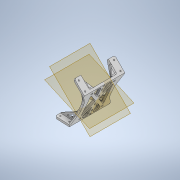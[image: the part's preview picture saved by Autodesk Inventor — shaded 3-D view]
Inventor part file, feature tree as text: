
AUTODESK INVENTOR PART (.ipt)
format: ipt  version: 2023 (Build 270158000, 158)  size: 826,880 bytes
history: native  units: mm
features: projected_geometry x20, sketch x13, extrude x11, fillet x6, reference x6, other x6, mirror x5, plane x4, hole x2, chamfer x1
ambient origin geometry x8: Origin, YZ Plane, XZ Plane, XY Plane, X Axis, Y Axis, Z Axis, Center Point
bodies: Solid1 (feature_tree)
feature tree (74):
  sketch  "Sketch1"  dims[d1=3.0mm d2=22.0mm]
  plane  "Work Plane1"
  extrude  "Extrusion1"  Depth=3.0mm
  hole  "Hole1"  [1 undecoded]
  hole  "Hole2"  [1 undecoded]
  sketch  "Sketch4"  dims[d8=2.0mm d9=6.0mm d10=4.0mm d11=2.0mm d12=90.0deg d13=20.0mm d14=0.0mm]
  plane  "Work Plane2"
  extrude  "Extrusion2"  Depth=10.0mm
  plane  "Work Plane3"
  mirror  "Mirror1"
  extrude  "Extrusion3"  Depth=2.0mm TaperAngle=0.0deg
  mirror  "Mirror2"
  extrude  "Extrusion4"  Depth=10.0mm
  extrude  "Extrusion5"  Depth=10.0mm
  plane  "Work Plane4"
  mirror  "Mirror3"
  chamfer  "Chamfer1"  Distance=2.0mm
  fillet  "Fillet1"  Radius=2.0mm
  extrude  "Extrusion6"  Depth=2.5mm
  fillet  "Fillet2"  Radius=2.5mm
  fillet  "Fillet3"  Radius=2.5mm
  fillet  "Fillet4"  Radius=2.5mm
  fillet  "Fillet5"  Radius=2.5mm
  fillet  "Fillet6"  Radius=500.0mm
  extrude  "Extrusion7"  Depth=2.0mm
  extrude  "Extrusion8"  Depth=3.0mm
  extrude  "Extrusion9"  Depth=2.0mm
  extrude  "Extrusion10"  Depth=2.0mm
  mirror  "Mirror4"
  mirror  "Mirror5"
  extrude  "Extrusion11"  Depth=3.0mm
  reference  "Reference1"
  reference  "Reference2"
  sketch  "Sketch2"  dims[d4=3.0mm d5=22.0mm]
  reference  "Reference3"
  reference  "Reference4"
  sketch  "Sketch3"  dims[d6=10.0mm d7=0.0mm]
  reference  "Reference5"
  reference  "Reference6"
  projected_geometry  "Projected Loop1"
  projected_geometry  "Projected Loop2"
  sketch  "Sketch5"  dims[d15=2.0mm d16=6.0mm d17=4.0mm d18=2.0mm d19=90.0deg d20=20.0mm d21=0.0mm d22=3.0mm]
  projected_geometry  "Projected Loop3"
  projected_geometry  "Projected Loop4"
  sketch  "Sketch6"  dims[d23=10.0mm d24=0.0mm d25=10.0mm]
  projected_geometry  "Projected Loop5"
  projected_geometry  "Projected Loop6"
  projected_geometry  "Projected Loop7"
  projected_geometry  "Projected Loop8"
  projected_geometry  "Projected Loop9"
  sketch  "Sketch7"  dims[d26=10.0mm d27=2.0mm d28=0.0mm]
  projected_geometry  "Projected Loop10"
  projected_geometry  "Projected Loop11"
  projected_geometry  "Projected Loop12"
  projected_geometry  "Projected Loop13"
  projected_geometry  "Projected Loop14"
  sketch  "Sketch8"  dims[d29=2.0mm d30=0.0mm d31=10.0mm]
  projected_geometry  "Projected Loop15"
  sketch  "Sketch9"  dims[d32=10.0mm d33=15.0mm]
  projected_geometry  "Projected Loop16"
  sketch  "Sketch10"  dims[d34=15.0mm d35=2.0mm d36=0.0mm]
  projected_geometry  "Projected Loop17"
  sketch  "Sketch11"  dims[d37=2.0mm d38=2.0mm d39=45.0deg d40=2.0mm]
  projected_geometry  "Projected Loop18"
  sketch  "Sketch12"  dims[d41=2.5mm d42=2.5mm d43=2.5mm d44=2.5mm d45=2.5mm d46=2.5mm d47=500.0mm d48=0.0mm]
  projected_geometry  "Projected Loop19"
  sketch  "Sketch13"  dims[d49=0.7mm d50=2.0mm d51=20.0mm d52=2.0mm d53=2.0mm d54=4.0mm d55=7.0mm d56=4.0mm d57=7.0mm d58=3.0mm d59=3.0mm d60=3.0mm d61=3.0mm d62=500.0mm d63=0.0mm d64=35.0mm d65=47.0mm d66=3.0mm d67=3.0mm d68=3.0mm d69=3.0mm d70=20.0mm d71=0.0mm d72=4.0mm d73=2.0mm d74=2.0mm d75=2.0mm d76=2.0mm d78=4.0mm d79=2.0mm d80=1.0mm d81=20.0mm d82=0.0mm d83=30.0deg d84=4.0mm d85=4.0mm d86=4.0mm d87=1.0mm d88=2.0mm d89=20.0mm d90=0.0mm d91=12.0mm d92=12.0mm d93=3.0mm d94=3.0mm d95=20.0mm d96=0.0mm]
  projected_geometry  "Projected Loop20"
  parser-record x1  (decoder bookkeeping rows leaked as tree rows — omitted from the tree; the rows remain in map.json)
  other  "body_8d_1.iam"
  other  "leg_1_2d_MIR:2"
  other  "leg_holder_2_MIR:1"
  other  "leg_2d_1:1"
  other  "leg_holder_2:1"
note: 2 required parameter values undecoded (feature->parameter linkage not recoverable at this tier; creation-order binding heuristic only, values carry confidence <= 0.55)
note: 1 file-system path scrubbed to <path> (originals preserved in map.json)
